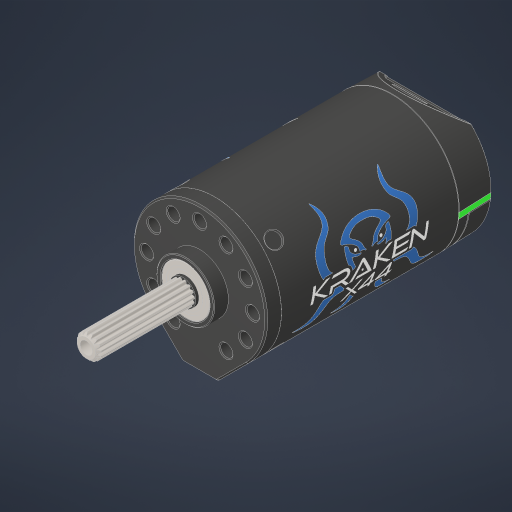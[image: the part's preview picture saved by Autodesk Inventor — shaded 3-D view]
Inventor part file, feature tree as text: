
AUTODESK INVENTOR PART (.ipt)
format: ipt  version: 2023.4 (Build 274418000, 418)  size: 6,377,984 bytes
history: native  units: in
note: dims shown in document units (in); Inventor stores cm internally (conversion verified against a paired STEP export)
features: chamfer x1, boolean_combine x1
ambient origin geometry x8: Origin, YZ Plane, XZ Plane, XY Plane, X Axis, Y Axis, Z Axis, Center Point
bodies: Solid1 (feature_tree), Solid2 (feature_tree)
feature tree (2):
  chamfer  "Chamfer5"  [1 undecoded]
  boolean_combine  "Combine5"
note: 1 required parameter value undecoded (feature->parameter linkage not recoverable at this tier; creation-order binding heuristic only, values carry confidence <= 0.55)
